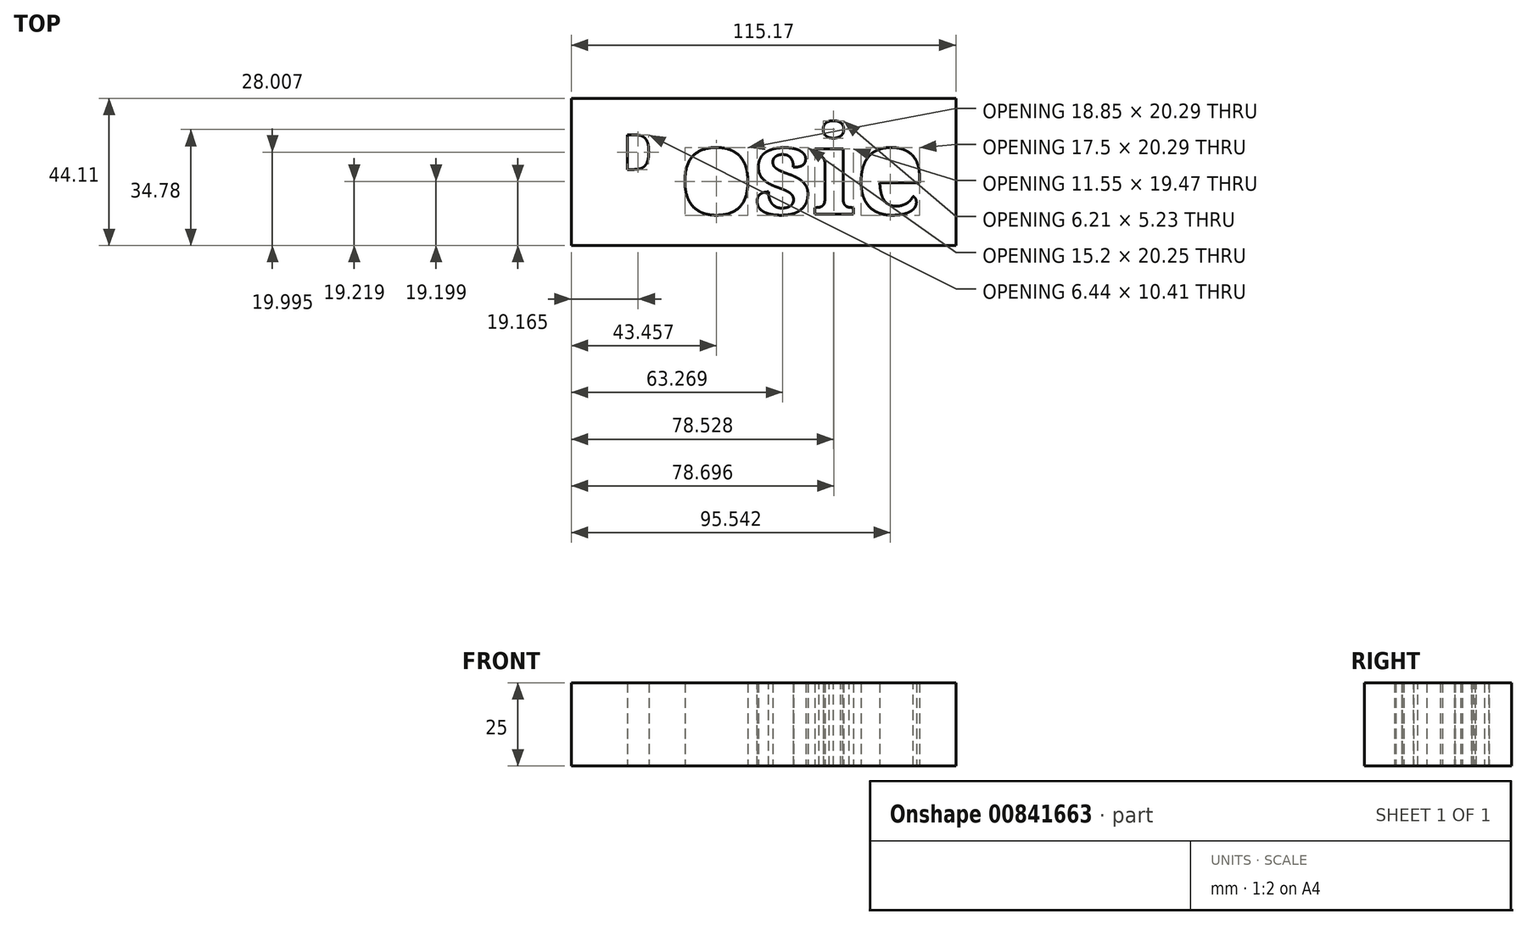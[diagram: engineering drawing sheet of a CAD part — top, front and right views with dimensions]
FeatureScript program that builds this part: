
annotation { "Feature Type Name" : "Feature", "Feature Type Description" : "" }
export const myFeature = defineFeature(function(context is Context, id is Id, definition is map)
    precondition{}
    {
        {
            var Q0;
            Q0=qCreatedBy(makeId("Top.planeOp"),FACE);
            var sketch = newSketch(context, id + "F0", { "sketchPlane" : qUnion([Q0])});
            skText(sketch, "E0", { "text": "Rosie ", "fontName": "NotoSerif-Bold.ttf"});
            skLineSegment(sketch, "E1", {"start": v(-63.2, 18.8) * mm, "end": v(-63.2, -25.31) * mm});
            skLineSegment(sketch, "E2", {"start": v(-63.2, -25.31) * mm, "end": v(51.96, -25.31) * mm});
            skLineSegment(sketch, "E3", {"start": v(51.96, -25.31) * mm, "end": v(51.96, 18.8) * mm});
            skLineSegment(sketch, "E4", {"start": v(51.96, 18.8) * mm, "end": v(-63.2, 18.8) * mm});
            skLineSegment(sketch, "E5", {"start": v(-63.2, 18.8) * mm, "end": v(-63.2, 18.8) * mm});
            const initialGuessF0  = {"E0": [-0.05656, -0.01588, 1, 0, 0.02615]};
            skSetInitialGuess(sketch, initialGuessF0);
            skSolve(sketch);
        }
        {
            var Q0;
            Q0 = qSketchRegion(id + "F0", true);
            var Q1;
            Q1=makeQuery(id+"F0.imprint","IMPRINT",FACE,{"disambiguationData":[TD([[makeQuery(id+"F0.imprint","IMPRINT",EDGE,{"derivedFrom":sQuery(id+"F0.wireOp",EDGE,"E0.sketch_text.stroke-0")}),-1.0]])]});
            extrude(context, id + "F1", {"entities" : qUnion([Q0, Q1]), "depth" : 25 * mm, "offsetDistance" : 25 * mm});
        }
    });
